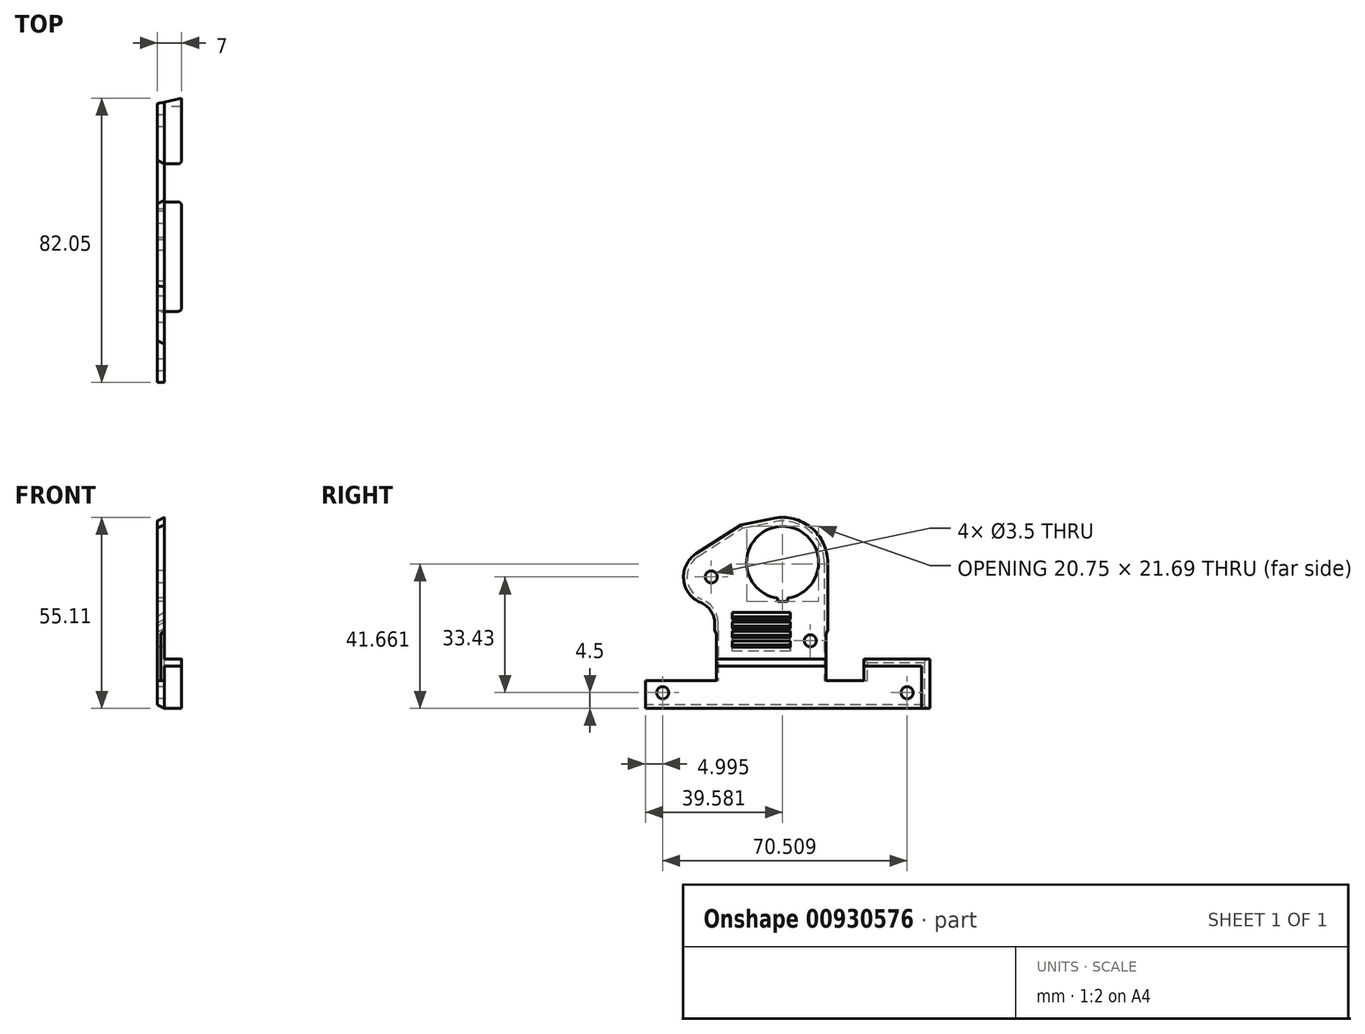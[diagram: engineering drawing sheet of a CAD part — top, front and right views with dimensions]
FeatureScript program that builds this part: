
annotation { "Feature Type Name" : "Feature", "Feature Type Description" : "" }
export const myFeature = defineFeature(function(context is Context, id is Id, definition is map)
    precondition{}
    {
        {
            var Q0;
            Q0=qCreatedBy(makeId("Right.planeOp"),FACE);
            var sketch = newSketch(context, id + "F0", { "sketchPlane" : qUnion([Q0])});
            skLineSegment(sketch, "E0", {"start": v(0, 0) * mm, "end": v(0, 35.08) * mm, "construction": true});
            skLineSegment(sketch, "E1", {"start": v(-91.61, 0) * mm, "end": v(0, 0) * mm, "construction": true});
            skLineSegment(sketch, "E2", {"start": v(-91.61, 0) * mm, "end": v(-91.61, 16.1) * mm, "construction": true});
            skLineSegment(sketch, "E3", {"start": v(0, 13) * mm, "end": v(-91.61, 13) * mm, "construction": true});
            skLineSegment(sketch, "E4", {"start": v(0, 10) * mm, "end": v(-91.61, 10) * mm, "construction": true});
            skLineSegment(sketch, "E5", {"start": v(0, 0) * mm, "end": v(0, -3) * mm, "construction": true});
            skLineSegment(sketch, "E6", {"start": v(0, -3) * mm, "end": v(-19.03, -3) * mm, "construction": true});
            skLineSegment(sketch, "E7", {"start": v(-19.03, 0) * mm, "end": v(-19.03, -5.5) * mm, "construction": true});
            skLineSegment(sketch, "E8", {"start": v(-19.03, -5.5) * mm, "end": v(-29.03, -5.5) * mm, "construction": true});
            skLineSegment(sketch, "E9", {"start": v(-29.03, -5.5) * mm, "end": v(-29.03, 0) * mm, "construction": true});
            skLineSegment(sketch, "E10", {"start": v(-61.61, 0) * mm, "end": v(-61.61, -5.5) * mm, "construction": true});
            skLineSegment(sketch, "E11", {"start": v(-61.61, -5.5) * mm, "end": v(-81.61, -5.5) * mm, "construction": true});
            skLineSegment(sketch, "E12", {"start": v(-81.61, -5.5) * mm, "end": v(-81.61, 0) * mm, "construction": true});
            skLineSegment(sketch, "E13", {"start": v(-29.03, -3) * mm, "end": v(-61.61, -3) * mm, "construction": true});
            skLineSegment(sketch, "E14", {"start": v(-91.61, 0) * mm, "end": v(-91.61, -3) * mm, "construction": true});
            skLineSegment(sketch, "E15", {"start": v(-91.61, -3) * mm, "end": v(-81.61, -3) * mm, "construction": true});
            skLineSegment(sketch, "E16", {"start": v(-19.03, 0) * mm, "end": v(-19.03, 2) * mm, "construction": true});
            skLineSegment(sketch, "E17", {"start": v(-19.03, 2) * mm, "end": v(-29.03, 2) * mm, "construction": true});
            skLineSegment(sketch, "E18", {"start": v(-29.03, 2) * mm, "end": v(-29.03, 0) * mm, "construction": true});
            skLineSegment(sketch, "E19", {"start": v(-61.61, 0) * mm, "end": v(-61.61, 2) * mm, "construction": true});
            skLineSegment(sketch, "E20", {"start": v(-61.61, 2) * mm, "end": v(-81.61, 2) * mm, "construction": true});
            skLineSegment(sketch, "E21", {"start": v(-81.61, 2) * mm, "end": v(-81.61, 0) * mm, "construction": true});
            skLineSegment(sketch, "E22", {"start": v(0, 35.08) * mm, "end": v(-26.06, 45.64) * mm, "construction": true});
            skLineSegment(sketch, "E23", {"start": v(-26.06, 45.64) * mm, "end": v(-54.7, 40) * mm, "construction": true});
            skLineSegment(sketch, "E24", {"start": v(-54.7, 40) * mm, "end": v(-91.61, 16.1) * mm, "construction": true});
            skSolve(sketch);
        }
        {
            var Q0;
            Q0=qCreatedBy(makeId("Right.planeOp"),FACE);
            var sketch = newSketch(context, id + "F1", { "sketchPlane" : qUnion([Q0])});
            skLineSegment(sketch, "E25", {"start": v(-29.03, 27.6) * mm, "end": v(-29.03, 8) * mm});
            skLineSegment(sketch, "E26", {"start": v(-61.61, 10) * mm, "end": v(-61.61, 8) * mm});
            skArc(sketch, "E27", {"start": v(-29.03, 27.6) * mm, "mid": v(-33.77, 37.65) * mm, "end": v(-44.54, 40.36) * mm});
            skLineSegment(sketch, "E28", {"start": v(-44.54, 40.36) * mm, "end": v(-54.08, 38.48) * mm});
            skLineSegment(sketch, "E29", {"start": v(-54.08, 38.48) * mm, "end": v(-66.96, 30.15) * mm});
            skArc(sketch, "E30", {"start": v(-66.96, 30.15) * mm, "mid": v(-70.58, 22.7) * mm, "end": v(-65.66, 16.03) * mm});
            skArc(sketch, "E31", {"start": v(-61.61, 10) * mm, "mid": v(-62.72, 13.63) * mm, "end": v(-65.66, 16.03) * mm});
            skLineSegment(sketch, "E32", {"start": v(-42.03, 27.6) * mm, "end": v(-62.6, 23.43) * mm, "construction": true});
            skLineSegment(sketch, "E33", {"start": v(-49.3, 39.42) * mm, "end": v(-49.62, 41) * mm, "construction": true});
            skLineSegment(sketch, "E34", {"start": v(-60.52, 34.31) * mm, "end": v(-61.39, 35.66) * mm, "construction": true});
            skLineSegment(sketch, "E35", {"start": v(-42.03, 27.6) * mm, "end": v(-44.93, 41.92) * mm, "construction": true});
            skLineSegment(sketch, "E36", {"start": v(-42.03, 27.6) * mm, "end": v(-42.03, 13) * mm, "construction": true});
            skLineSegment(sketch, "E37", {"start": v(-29.03, 8) * mm, "end": v(-29.53, 7.13) * mm});
            skLineSegment(sketch, "E38", {"start": v(-29.53, 7.13) * mm, "end": v(-29.53, -6.5) * mm});
            skLineSegment(sketch, "E39", {"start": v(-29.53, -6.5) * mm, "end": v(-18.53, -6.5) * mm});
            skLineSegment(sketch, "E40", {"start": v(-18.53, -6.5) * mm, "end": v(-18.53, -0.3) * mm});
            skLineSegment(sketch, "E41", {"start": v(-18.53, -0.3) * mm, "end": v(0, -0.3) * mm});
            skLineSegment(sketch, "E42", {"start": v(0, -0.3) * mm, "end": v(0, -14.5) * mm});
            skLineSegment(sketch, "E43", {"start": v(0, -14.5) * mm, "end": v(-81.61, -14.5) * mm});
            skLineSegment(sketch, "E44", {"start": v(-81.61, -14.5) * mm, "end": v(-81.61, -6.5) * mm});
            skLineSegment(sketch, "E45", {"start": v(-81.61, -6.5) * mm, "end": v(-61.11, -6.5) * mm});
            skLineSegment(sketch, "E46", {"start": v(-61.11, -6.5) * mm, "end": v(-61.11, 7.13) * mm});
            skLineSegment(sketch, "E47", {"start": v(-61.11, 7.13) * mm, "end": v(-61.61, 8) * mm});
            skCircle(sketch, "E48", {"center": v(-62.6, 23.43) * mm, "radius": 1.75 * mm});
            skArc(sketch, "E49", {"start": v(-40.53, 17.32) * mm, "mid": v(-42.03, 38) * mm, "end": v(-43.53, 17.32) * mm});
            skCircle(sketch, "E50", {"center": v(-34.03, 5) * mm, "radius": 1.75 * mm});
            skLineSegment(sketch, "E51", {"start": v(-40.53, 17.32) * mm, "end": v(-40.53, 16.32) * mm});
            skLineSegment(sketch, "E52", {"start": v(-40.53, 16.32) * mm, "end": v(-43.53, 16.32) * mm});
            skLineSegment(sketch, "E53", {"start": v(-43.53, 16.32) * mm, "end": v(-43.53, 17.32) * mm});
            skCircle(sketch, "E54", {"center": v(-42.03, 27.6) * mm, "radius": 10.1 * mm, "construction": true});
            skSolve(sketch);
        }
        {
            var Q0;
            Q0=qSketchRegion(id+"F1",true);
            extrude(context, id + "F2", {"entities" : qUnion([Q0]), "depth" : 2 * mm, "offsetDistance" : 25 * mm});
        }
        {
            var Q0;
            Q0=makeQuery(id+"F2.opExtrude","SWEPT_FACE",FACE,{"disambiguationData":[OSD([sQuery(id+"F1.wireOp",EDGE,"E45")])]});
            var sketch = newSketch(context, id + "F3", { "sketchPlane" : qUnion([Q0])});
            skLineSegment(sketch, "E55", {"start": v(2, -61.61) * mm, "end": v(0, -60.61) * mm});
            skLineSegment(sketch, "E56", {"start": v(2, -61.61) * mm, "end": v(0, -61.61) * mm});
            skLineSegment(sketch, "E57", {"start": v(0, -61.61) * mm, "end": v(0, -60.61) * mm});
            skSolve(sketch);
        }
        {
            var Q0;
            Q0=qSketchRegion(id+"F3",true);
            extrude(context, id + "F4", {"entities" : qUnion([Q0]), "operationType" : NewBodyOperationType.REMOVE, "depth" : 14.5 * mm, "offsetDistance" : 25 * mm});
        }
        {
            var Q0;
            Q0=makeQuery(id+"F2.opExtrude","CAP_EDGE",EDGE,{"disambiguationData":[OSD([sQuery(id+"F1.wireOp",EDGE,"E30")])],"isStart":true});
            var Q1;
            Q1=makeQuery(id+"F2.opExtrude","CAP_EDGE",EDGE,{"disambiguationData":[OSD([sQuery(id+"F1.wireOp",EDGE,"E28")])],"isStart":true});
            var Q2;
            Q2=makeQuery(id+"F2.opExtrude","CAP_EDGE",EDGE,{"disambiguationData":[OSD([sQuery(id+"F1.wireOp",EDGE,"E40")])],"isStart":true});
            var Q3;
            Q3=makeQuery(id+"F2.opExtrude","CAP_EDGE",EDGE,{"disambiguationData":[OSD([sQuery(id+"F1.wireOp",EDGE,"E41")])],"isStart":true});
            var Q4;
            Q4=makeQuery(id+"F2.opExtrude","CAP_EDGE",EDGE,{"disambiguationData":[OSD([sQuery(id+"F1.wireOp",EDGE,"E43")])],"isStart":true});
            chamfer(context, id + "F5", {"entities" : qUnion([Q0, Q1, Q2, Q3, Q4]), "chamferType" : ChamferType.TWO_OFFSETS, "width1" : 2 * mm, "oppositeDirection" : false, "width2" : 1 * mm, "tangentPropagation" : true});
        }
        {
            var Q0;
            Q0=makeQuery(id+"F2.opExtrude","CAP_FACE",FACE,{"disambiguationData":[OSD([sQuery(id+"F1.wireOp",EDGE,"E25"),sQuery(id+"F1.wireOp",EDGE,"E26"),sQuery(id+"F1.wireOp",EDGE,"E27"),sQuery(id+"F1.wireOp",EDGE,"E28"),sQuery(id+"F1.wireOp",EDGE,"E29"),sQuery(id+"F1.wireOp",EDGE,"E30"),sQuery(id+"F1.wireOp",EDGE,"E31"),sQuery(id+"F1.wireOp",EDGE,"E37"),sQuery(id+"F1.wireOp",EDGE,"E38"),sQuery(id+"F1.wireOp",EDGE,"E39"),sQuery(id+"F1.wireOp",EDGE,"E40"),sQuery(id+"F1.wireOp",EDGE,"E41"),sQuery(id+"F1.wireOp",EDGE,"E42"),sQuery(id+"F1.wireOp",EDGE,"E43"),sQuery(id+"F1.wireOp",EDGE,"E44"),sQuery(id+"F1.wireOp",EDGE,"E45"),sQuery(id+"F1.wireOp",EDGE,"E46"),sQuery(id+"F1.wireOp",EDGE,"E47"),sQuery(id+"F1.wireOp",EDGE,"E48"),sQuery(id+"F1.wireOp",EDGE,"E49"),sQuery(id+"F1.wireOp",EDGE,"E50")])],"isStart":false});
            var sketch = newSketch(context, id + "F6", { "sketchPlane" : qUnion([Q0])});
            skLineSegment(sketch, "E58", {"start": v(-18.53, -0.3) * mm, "end": v(-18.53, -2.3) * mm});
            skLineSegment(sketch, "E59", {"start": v(-18.53, -2.3) * mm, "end": v(-2, -2.3) * mm});
            skLineSegment(sketch, "E60", {"start": v(-2, -2.3) * mm, "end": v(-2, -14.5) * mm});
            skLineSegment(sketch, "E61", {"start": v(-2, -14.5) * mm, "end": v(0, -14.5) * mm});
            skLineSegment(sketch, "E62", {"start": v(0, -14.5) * mm, "end": v(0, -0.3) * mm});
            skLineSegment(sketch, "E63", {"start": v(0, -0.3) * mm, "end": v(-18.53, -0.3) * mm});
            skLineSegment(sketch, "E64.bottom", {"start": v(-29.53, -0.3) * mm, "end": v(-61.11, -0.3) * mm});
            skLineSegment(sketch, "E64.top", {"start": v(-29.53, -2.3) * mm, "end": v(-61.11, -2.3) * mm});
            skLineSegment(sketch, "E64.left", {"start": v(-29.53, -0.3) * mm, "end": v(-29.53, -2.3) * mm});
            skLineSegment(sketch, "E64.right", {"start": v(-61.11, -0.3) * mm, "end": v(-61.11, -2.3) * mm});
            skSolve(sketch);
        }
        {
            var Q0;
            Q0=qSketchRegion(id+"F6",true);
            extrude(context, id + "F7", {"entities" : qUnion([Q0]), "operationType" : NewBodyOperationType.ADD, "depth" : 5 * mm, "offsetDistance" : 25 * mm});
        }
        {
            var Q0;
            Q0=makeQuery(id+"F7.opExtrude","CAP_EDGE",EDGE,{"disambiguationData":[OSD([sQuery(id+"F6.wireOp",EDGE,"E64.right")])],"isStart":false});
            var Q1;
            Q1=makeQuery(id+"F7.opExtrude","CAP_EDGE",EDGE,{"disambiguationData":[OSD([sQuery(id+"F6.wireOp",EDGE,"E64.left")])],"isStart":false});
            var Q2;
            Q2=makeQuery(id+"F7.opExtrude","CAP_EDGE",EDGE,{"disambiguationData":[OSD([sQuery(id+"F6.wireOp",EDGE,"E58")])],"isStart":false});
            fillet(context, id + "F8", {"entities" : qUnion([Q0, Q1, Q2]), "radius" : 1 * mm, "tangentPropagation" : true, "allowEdgeOverflow" : false});
        }
        {
            var Q0;
            Q0=makeQuery(id+"F7.opExtrude","SWEPT_FACE",FACE,{"disambiguationData":[OSD([sQuery(id+"F6.wireOp",EDGE,"E63")])]});
            var sketch = newSketch(context, id + "F9", { "sketchPlane" : qUnion([Q0])});
            skLineSegment(sketch, "E65", {"start": v(5, -18.53) * mm, "end": v(5, 0) * mm, "construction": true});
            skLineSegment(sketch, "E66", {"start": v(5, 0) * mm, "end": v(0, 0) * mm});
            skLineSegment(sketch, "E67", {"start": v(0, 0) * mm, "end": v(0, -1.1) * mm});
            skLineSegment(sketch, "E68", {"start": v(0, -1.1) * mm, "end": v(5, 0) * mm});
            skSolve(sketch);
        }
        {
            var Q0;
            Q0=qSketchRegion(id+"F9",true);
            var Q1;
            Q1=makeQuery(id+"F7.opExtrude","SWEPT_FACE",FACE,{"disambiguationData":[OSD([sQuery(id+"F6.wireOp",EDGE,"E61")])]});
            extrude(context, id + "F10", {"entities" : qUnion([Q0]), "operationType" : NewBodyOperationType.REMOVE, "endBound" : BoundingType.UP_TO_SURFACE, "oppositeDirection" : true, "depth" : 25 * mm, "endBoundEntityFace" : qUnion([Q1]), "offsetDistance" : 25 * mm});
        }
        {
            var Q0;
            Q0=makeQuery(id+"F7.opExtrude","SWEPT_FACE",FACE,{"disambiguationData":[OSD([sQuery(id+"F6.wireOp",EDGE,"E63")])]});
            var sketch = newSketch(context, id + "F11", { "sketchPlane" : qUnion([Q0])});
            skLineSegment(sketch, "E69", {"start": v(5, 0) * mm, "end": v(7, 0) * mm});
            skLineSegment(sketch, "E70", {"start": v(7, 0) * mm, "end": v(7, 0.44) * mm});
            skLineSegment(sketch, "E71", {"start": v(7, 0.44) * mm, "end": v(5, 0) * mm});
            skSolve(sketch);
        }
        {
            var Q0;
            Q0=qSketchRegion(id+"F11",true);
            var Q1;
            Q1=makeQuery(id+"F7.opExtrude","SWEPT_FACE",FACE,{"disambiguationData":[OSD([sQuery(id+"F6.wireOp",EDGE,"E61")])]});
            extrude(context, id + "F12", {"entities" : qUnion([Q0]), "operationType" : NewBodyOperationType.ADD, "endBound" : BoundingType.UP_TO_SURFACE, "oppositeDirection" : true, "depth" : 25 * mm, "endBoundEntityFace" : qUnion([Q1]), "offsetDistance" : 25 * mm});
        }
        {
            var Q0;
            Q0=makeQuery(id+"F2.opExtrude","CAP_FACE",FACE,{"disambiguationData":[OSD([sQuery(id+"F1.wireOp",EDGE,"E25"),sQuery(id+"F1.wireOp",EDGE,"E26"),sQuery(id+"F1.wireOp",EDGE,"E27"),sQuery(id+"F1.wireOp",EDGE,"E28"),sQuery(id+"F1.wireOp",EDGE,"E29"),sQuery(id+"F1.wireOp",EDGE,"E30"),sQuery(id+"F1.wireOp",EDGE,"E31"),sQuery(id+"F1.wireOp",EDGE,"E37"),sQuery(id+"F1.wireOp",EDGE,"E38"),sQuery(id+"F1.wireOp",EDGE,"E39"),sQuery(id+"F1.wireOp",EDGE,"E40"),sQuery(id+"F1.wireOp",EDGE,"E41"),sQuery(id+"F1.wireOp",EDGE,"E42"),sQuery(id+"F1.wireOp",EDGE,"E43"),sQuery(id+"F1.wireOp",EDGE,"E44"),sQuery(id+"F1.wireOp",EDGE,"E45"),sQuery(id+"F1.wireOp",EDGE,"E46"),sQuery(id+"F1.wireOp",EDGE,"E47"),sQuery(id+"F1.wireOp",EDGE,"E48"),sQuery(id+"F1.wireOp",EDGE,"E49"),sQuery(id+"F1.wireOp",EDGE,"E50")])],"isStart":true});
            var sketch = newSketch(context, id + "F13", { "sketchPlane" : qUnion([Q0])});
            skLineSegment(sketch, "E72", {"start": v(39.78, 2) * mm, "end": v(56.61, 2) * mm});
            skLineSegment(sketch, "E73", {"start": v(56.61, 2) * mm, "end": v(56.61, 13.12) * mm});
            skLineSegment(sketch, "E74", {"start": v(56.61, 13.12) * mm, "end": v(39.78, 13.12) * mm});
            skLineSegment(sketch, "E75", {"start": v(39.78, 2) * mm, "end": v(39.78, 13.12) * mm});
            skSolve(sketch);
        }
        {
            var Q0;
            Q0=qSketchRegion(id+"F13",true);
            extrude(context, id + "F14", {"entities" : qUnion([Q0]), "operationType" : NewBodyOperationType.REMOVE, "endBound" : BoundingType.UP_TO_NEXT, "oppositeDirection" : true, "depth" : 1 * mm, "offsetDistance" : 25 * mm});
        }
        {
            var Q0;
            Q0=makeQuery(id+"F2.opExtrude","CAP_FACE",FACE,{"disambiguationData":[OSD([sQuery(id+"F1.wireOp",EDGE,"E25"),sQuery(id+"F1.wireOp",EDGE,"E26"),sQuery(id+"F1.wireOp",EDGE,"E27"),sQuery(id+"F1.wireOp",EDGE,"E28"),sQuery(id+"F1.wireOp",EDGE,"E29"),sQuery(id+"F1.wireOp",EDGE,"E30"),sQuery(id+"F1.wireOp",EDGE,"E31"),sQuery(id+"F1.wireOp",EDGE,"E37"),sQuery(id+"F1.wireOp",EDGE,"E38"),sQuery(id+"F1.wireOp",EDGE,"E39"),sQuery(id+"F1.wireOp",EDGE,"E40"),sQuery(id+"F1.wireOp",EDGE,"E41"),sQuery(id+"F1.wireOp",EDGE,"E42"),sQuery(id+"F1.wireOp",EDGE,"E43"),sQuery(id+"F1.wireOp",EDGE,"E44"),sQuery(id+"F1.wireOp",EDGE,"E45"),sQuery(id+"F1.wireOp",EDGE,"E46"),sQuery(id+"F1.wireOp",EDGE,"E47"),sQuery(id+"F1.wireOp",EDGE,"E48"),sQuery(id+"F1.wireOp",EDGE,"E49"),sQuery(id+"F1.wireOp",EDGE,"E50"),sQuery(id+"F1.wireOp",EDGE,"E51"),sQuery(id+"F1.wireOp",EDGE,"E52"),sQuery(id+"F1.wireOp",EDGE,"E53")])],"isStart":true});
            var sketch = newSketch(context, id + "F15", { "sketchPlane" : qUnion([Q0])});
            skCircle(sketch, "E76", {"center": v(6.1, -10) * mm, "radius": 1.75 * mm});
            skCircle(sketch, "E77", {"center": v(76.61, -10) * mm, "radius": 1.75 * mm});
            skLineSegment(sketch, "E78", {"start": v(6.1, -10) * mm, "end": v(76.61, -10) * mm, "construction": true});
            skSolve(sketch);
        }
        {
            var Q0;
            Q0=qSketchRegion(id+"F15",true);
            extrude(context, id + "F16", {"entities" : qUnion([Q0]), "operationType" : NewBodyOperationType.REMOVE, "endBound" : BoundingType.UP_TO_NEXT, "oppositeDirection" : true, "depth" : 25 * mm, "offsetDistance" : 25 * mm});
        }
        {
            var Q0;
            Q0=makeQuery(id+"F14.boolean.opBoolean","COPY",FACE,{"derivedFrom":makeQuery(id+"F14.opExtrude","SWEPT_FACE",FACE,{"disambiguationData":[OSD([sQuery(id+"F13.wireOp",EDGE,"E73")])]})});
            var sketch = newSketch(context, id + "F17", { "sketchPlane" : qUnion([Q0])});
            skLineSegment(sketch, "E79", {"start": v(0, 7.56) * mm, "end": v(-2, 7.56) * mm, "construction": true});
            skLineSegment(sketch, "E80", {"start": v(-1, 13.12) * mm, "end": v(-1, 2) * mm, "construction": true});
            skLineSegment(sketch, "E81", {"start": v(0, 7.44) * mm, "end": v(-2, 8.6) * mm});
            skLineSegment(sketch, "E82", {"start": v(-2, 8.6) * mm, "end": v(-2, 7.67) * mm});
            skLineSegment(sketch, "E83", {"start": v(-2, 7.67) * mm, "end": v(0, 6.52) * mm});
            skLineSegment(sketch, "E84", {"start": v(0, 6.52) * mm, "end": v(0, 7.44) * mm});
            skLineSegment(sketch, "E85", {"start": v(0, 9.24) * mm, "end": v(0, 10.16) * mm});
            skLineSegment(sketch, "E86", {"start": v(0, 10.16) * mm, "end": v(-2, 11.32) * mm});
            skLineSegment(sketch, "E87", {"start": v(-2, 11.32) * mm, "end": v(-2, 10.4) * mm});
            skLineSegment(sketch, "E88", {"start": v(-2, 10.4) * mm, "end": v(0, 9.24) * mm});
            skLineSegment(sketch, "E89", {"start": v(-2, 13.12) * mm, "end": v(0, 11.96) * mm});
            skLineSegment(sketch, "E90", {"start": v(0, 11.96) * mm, "end": v(0, 13.12) * mm});
            skLineSegment(sketch, "E91", {"start": v(0, 4.72) * mm, "end": v(0, 3.8) * mm});
            skLineSegment(sketch, "E92", {"start": v(0, 3.8) * mm, "end": v(-2, 4.95) * mm});
            skLineSegment(sketch, "E93", {"start": v(-2, 4.95) * mm, "end": v(-2, 5.88) * mm});
            skLineSegment(sketch, "E94", {"start": v(-2, 5.88) * mm, "end": v(0, 4.72) * mm});
            skLineSegment(sketch, "E95", {"start": v(0, 7.44) * mm, "end": v(0, 7.56) * mm, "construction": true});
            skLineSegment(sketch, "E96", {"start": v(-2, 7.56) * mm, "end": v(-2, 7.67) * mm, "construction": true});
            skLineSegment(sketch, "E97", {"start": v(0, 2) * mm, "end": v(-2, 3.15) * mm});
            skLineSegment(sketch, "E98", {"start": v(-2, 3.15) * mm, "end": v(-2, 2) * mm});
            skLineSegment(sketch, "E99", {"start": v(-2, 2) * mm, "end": v(0, 2) * mm});
            skLineSegment(sketch, "E100", {"start": v(0, 13.12) * mm, "end": v(-2, 13.12) * mm});
            skLineSegment(sketch, "E101", {"start": v(0, 11.96) * mm, "end": v(-0.78, 10.61) * mm, "construction": true});
            skLineSegment(sketch, "E102", {"start": v(0, 9.24) * mm, "end": v(-0.78, 7.9) * mm, "construction": true});
            skLineSegment(sketch, "E103", {"start": v(0, 6.52) * mm, "end": v(-0.78, 5.17) * mm, "construction": true});
            skLineSegment(sketch, "E104", {"start": v(0, 3.8) * mm, "end": v(-0.78, 2.45) * mm, "construction": true});
            skSolve(sketch);
        }
        {
            var Q0;
            Q0=qSketchRegion(id+"F17",true);
            extrude(context, id + "F18", {"entities" : qUnion([Q0]), "operationType" : NewBodyOperationType.ADD, "endBound" : BoundingType.UP_TO_NEXT, "depth" : 25 * mm, "offsetDistance" : 25 * mm});
        }
    });
